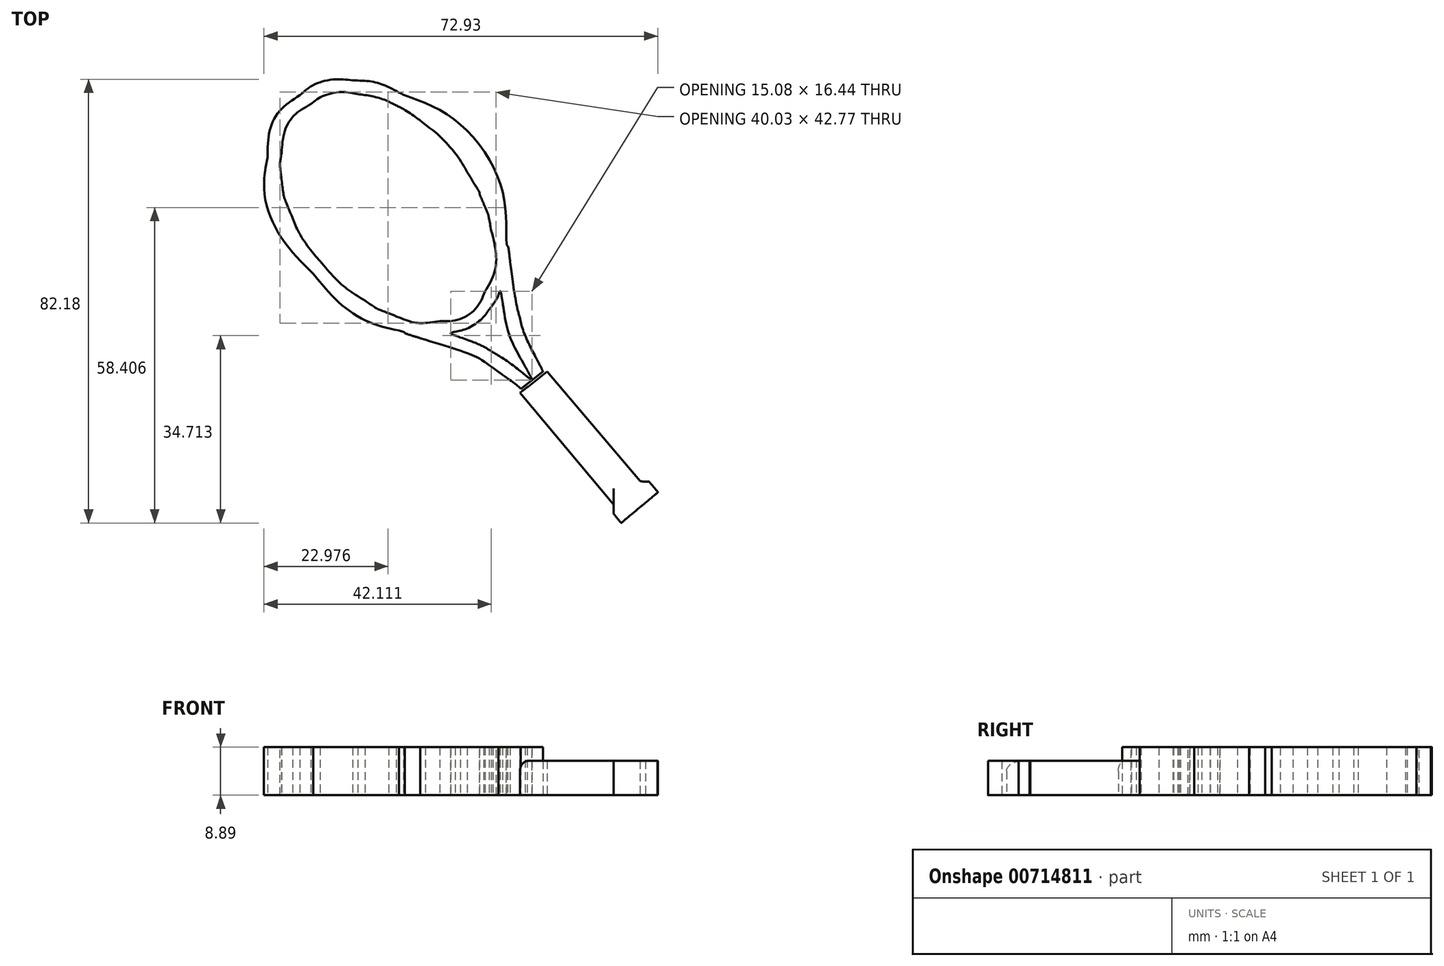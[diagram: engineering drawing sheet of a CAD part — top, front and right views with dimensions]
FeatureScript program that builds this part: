
annotation { "Feature Type Name" : "Feature", "Feature Type Description" : "" }
export const myFeature = defineFeature(function(context is Context, id is Id, definition is map)
    precondition{}
    {
        {
            var Q0;
            Q0=qCreatedBy(makeId("Top.planeOp"),FACE);
            var sketch = newSketch(context, id + "F0", { "sketchPlane" : qUnion([Q0])});
            skFitSpline(sketch, "E0", {"points": [v(14.84, -42.27) * mm, v(14.16, -41.44) * mm, v(14.13, -41.38) * mm, v(14.13, -40.56) * mm]});
            skFitSpline(sketch, "E1", {"points": [v(-3.07, -18.31) * mm, v(-3.2, -18.11) * mm, v(-5.86, -16.05) * mm, v(-7.2, -15.14) * mm]});
            skFitSpline(sketch, "E2", {"points": [v(-7.2, -15.14) * mm, v(-10.76, -12.67) * mm, v(-13.73, -11.39) * mm, v(-21.65, -8.9) * mm]});
            skFitSpline(sketch, "E3", {"points": [v(-21.65, -8.9) * mm, v(-23.19, -8.42) * mm, v(-24.48, -7.97) * mm, v(-24.53, -7.9) * mm]});
            skFitSpline(sketch, "E4", {"points": [v(-24.53, -7.9) * mm, v(-24.57, -7.83) * mm, v(-25.07, -7.64) * mm, v(-25.63, -7.48) * mm]});
            skFitSpline(sketch, "E5", {"points": [v(-25.63, -7.48) * mm, v(-31.35, -5.83) * mm, v(-36.86, -2.17) * mm, v(-41.46, 3.02) * mm]});
            skFitSpline(sketch, "E6", {"points": [v(-41.46, 3.02) * mm, v(-47.35, 9.65) * mm, v(-50.52, 17.71) * mm, v(-49.94, 24.59) * mm]});
            skFitSpline(sketch, "E7", {"points": [v(-49.94, 24.59) * mm, v(-49.52, 29.6) * mm, v(-47.6, 33.3) * mm, v(-43.94, 36.1) * mm]});
            skFitSpline(sketch, "E8", {"points": [v(-43.94, 36.1) * mm, v(-41.54, 37.93) * mm, v(-37.63, 39.02) * mm, v(-34.19, 38.83) * mm]});
            skFitSpline(sketch, "E9", {"points": [v(-34.19, 38.83) * mm, v(-30.86, 38.64) * mm, v(-28.26, 37.91) * mm, v(-24.79, 36.19) * mm]});
            skFitSpline(sketch, "E10", {"points": [v(-24.79, 36.19) * mm, v(-14.97, 31.3) * mm, v(-6.96, 20.04) * mm, v(-5.75, 9.4) * mm]});
            skFitSpline(sketch, "E11", {"points": [v(-5.75, 9.4) * mm, v(-5.68, 8.77) * mm, v(-5.56, 8.22) * mm, v(-5.5, 8.17) * mm]});
            skFitSpline(sketch, "E12", {"points": [v(-5.5, 8.17) * mm, v(-5.43, 8.13) * mm, v(-5.2, 6.8) * mm, v(-5, 5.21) * mm]});
            skFitSpline(sketch, "E13", {"points": [v(-5, 5.21) * mm, v(-4.54, 1.52) * mm, v(-3.77, -3) * mm, v(-3.29, -4.94) * mm]});
            skFitSpline(sketch, "E14", {"points": [v(-3.29, -4.94) * mm, v(-2.77, -6.97) * mm, v(-1.72, -9.61) * mm, v(-0.3, -12.38) * mm]});
            skFitSpline(sketch, "E15", {"points": [v(-0.3, -12.38) * mm, v(1.04, -15.03) * mm, v(1.07, -15.08) * mm, v(1.34, -14.85) * mm]});
            skFitSpline(sketch, "E16", {"points": [v(19.03, -35.32) * mm, v(19.21, -35.39) * mm, v(19.66, -35.44) * mm, v(20.03, -35.44) * mm]});
            skFitSpline(sketch, "E17", {"points": [v(20.03, -35.44) * mm, v(20.7, -35.44) * mm, v(20.71, -35.46) * mm, v(21.53, -36.43) * mm]});
            skFitSpline(sketch, "E18", {"points": [v(21.53, -36.43) * mm, v(21.99, -36.97) * mm, v(22.32, -37.46) * mm, v(22.26, -37.5) * mm]});
            skFitSpline(sketch, "E19", {"points": [v(22.26, -37.5) * mm, v(22.2, -37.56) * mm, v(20.8, -38.73) * mm, v(19.14, -40.1) * mm]});
            skFitSpline(sketch, "E20", {"points": [v(19.14, -40.1) * mm, v(17.48, -41.5) * mm, v(16, -42.74) * mm, v(15.83, -42.88) * mm]});
            skFitSpline(sketch, "E21", {"points": [v(15.83, -42.88) * mm, v(15.55, -43.13) * mm, v(15.54, -43.13) * mm, v(14.84, -42.27) * mm]});
            skLineSegment(sketch, "E22", {"start": v(14.13, -40.56) * mm, "end": v(14.13, -39.71) * mm});
            skFitSpline(sketch, "E23", {"points": [v(-1.88, -14.79) * mm, v(-4.5, -9.95) * mm, v(-5.63, -6.78) * mm, v(-6.46, -2.02) * mm]});
            skFitSpline(sketch, "E24", {"points": [v(-6.46, -2.02) * mm, v(-6.63, -1.02) * mm, v(-6.81, -0.2) * mm, v(-6.87, -0.2) * mm]});
            skFitSpline(sketch, "E25", {"points": [v(-6.87, -0.2) * mm, v(-6.92, -0.2) * mm, v(-7.03, -0.4) * mm, v(-7.11, -0.65) * mm]});
            skFitSpline(sketch, "E26", {"points": [v(-7.11, -0.65) * mm, v(-7.33, -1.27) * mm, v(-8.14, -2.58) * mm, v(-8.94, -3.6) * mm]});
            skFitSpline(sketch, "E27", {"points": [v(-8.94, -3.6) * mm, v(-10.3, -5.33) * mm, v(-12.99, -7.1) * mm, v(-15.18, -7.7) * mm]});
            skFitSpline(sketch, "E28", {"points": [v(-15.18, -7.7) * mm, v(-15.65, -7.82) * mm, v(-16.03, -7.97) * mm, v(-16.03, -8.01) * mm]});
            skFitSpline(sketch, "E29", {"points": [v(-16.03, -8.01) * mm, v(-16.03, -8.06) * mm, v(-15.22, -8.4) * mm, v(-14.22, -8.76) * mm]});
            skFitSpline(sketch, "E30", {"points": [v(-14.22, -8.76) * mm, v(-11.55, -9.74) * mm, v(-9.91, -10.49) * mm, v(-8.21, -11.5) * mm]});
            skFitSpline(sketch, "E31", {"points": [v(-8.21, -11.5) * mm, v(-6.48, -12.55) * mm, v(-4.04, -14.26) * mm, v(-2.27, -15.68) * mm]});
            skFitSpline(sketch, "E32", {"points": [v(-2.27, -15.68) * mm, v(-1.6, -16.22) * mm, v(-1.02, -16.64) * mm, v(-1, -16.6) * mm]});
            skFitSpline(sketch, "E33", {"points": [v(-1, -16.6) * mm, v(-0.96, -16.57) * mm, v(-1.36, -15.76) * mm, v(-1.88, -14.79) * mm]});
            skFitSpline(sketch, "E34", {"points": [v(-18.02, -5.76) * mm, v(-14.5, -5.4) * mm, v(-11.26, -3.26) * mm, v(-9.7, -0.23) * mm]});
            skFitSpline(sketch, "E35", {"points": [v(-9.7, -0.23) * mm, v(-8.02, 3) * mm, v(-7.63, 6.58) * mm, v(-8.5, 10.97) * mm]});
            skFitSpline(sketch, "E36", {"points": [v(-8.5, 10.97) * mm, v(-9.04, 13.74) * mm, v(-9.2, 14.3) * mm, v(-9.94, 16.01) * mm]});
            skFitSpline(sketch, "E37", {"points": [v(-9.94, 16.01) * mm, v(-10.35, 16.98) * mm, v(-10.69, 17.82) * mm, v(-10.69, 17.89) * mm]});
            skFitSpline(sketch, "E38", {"points": [v(-10.69, 17.89) * mm, v(-10.69, 18.02) * mm, v(-11.6, 19.6) * mm, v(-12.95, 21.8) * mm]});
            skFitSpline(sketch, "E39", {"points": [v(-12.95, 21.8) * mm, v(-14.73, 24.72) * mm, v(-18.08, 28.51) * mm, v(-20.73, 30.63) * mm]});
            skFitSpline(sketch, "E40", {"points": [v(-20.73, 30.63) * mm, v(-22.05, 31.68) * mm, v(-25.01, 33.64) * mm, v(-26.11, 34.18) * mm]});
            skFitSpline(sketch, "E41", {"points": [v(-26.11, 34.18) * mm, v(-28.1, 35.16) * mm, v(-30.67, 35.92) * mm, v(-33.24, 36.28) * mm]});
            skFitSpline(sketch, "E42", {"points": [v(-33.24, 36.28) * mm, v(-36.04, 36.68) * mm, v(-39.75, 35.9) * mm, v(-41.92, 34.45) * mm]});
            skFitSpline(sketch, "E43", {"points": [v(-41.92, 34.45) * mm, v(-44.96, 32.42) * mm, v(-46.77, 29.4) * mm, v(-47.36, 25.4) * mm]});
            skFitSpline(sketch, "E44", {"points": [v(-47.36, 25.4) * mm, v(-47.63, 23.56) * mm, v(-47.63, 22.79) * mm, v(-47.37, 20.67) * mm]});
            skFitSpline(sketch, "E45", {"points": [v(-47.37, 20.67) * mm, v(-47.03, 17.97) * mm, v(-46.62, 16.51) * mm, v(-45.27, 13.3) * mm]});
            skFitSpline(sketch, "E46", {"points": [v(-45.27, 13.3) * mm, v(-44.32, 11.03) * mm, v(-42.16, 7.65) * mm, v(-40.2, 5.38) * mm]});
            skFitSpline(sketch, "E47", {"points": [v(-40.2, 5.38) * mm, v(-37.55, 2.29) * mm, v(-35.22, 0.23) * mm, v(-31.93, -1.95) * mm]});
            skFitSpline(sketch, "E48", {"points": [v(-31.93, -1.95) * mm, v(-29.88, -3.3) * mm, v(-29.47, -3.52) * mm, v(-27.49, -4.29) * mm]});
            skFitSpline(sketch, "E49", {"points": [v(-27.49, -4.29) * mm, v(-23.61, -5.78) * mm, v(-21.51, -6.11) * mm, v(-18.02, -5.76) * mm]});
            skLineSegment(sketch, "E50", {"start": v(-18.02, -5.76) * mm, "end": v(-18.02, -5.76) * mm});
            skLineSegment(sketch, "E51", {"start": v(-3.07, -18.31) * mm, "end": v(1.34, -14.85) * mm});
            skLineSegment(sketch, "E52", {"start": v(-3.2, -19.01) * mm, "end": v(14.13, -39.71) * mm});
            skLineSegment(sketch, "E53", {"start": v(-3.07, -18.31) * mm, "end": v(-3.2, -19.01) * mm});
            skLineSegment(sketch, "E54", {"start": v(-3.2, -19.01) * mm, "end": v(1.84, -15.07) * mm});
            skLineSegment(sketch, "E55", {"start": v(1.84, -15.07) * mm, "end": v(19.03, -35.32) * mm});
            skLineSegment(sketch, "E56", {"start": v(-2.73, -18.65) * mm, "end": v(-3.07, -18.31) * mm});
            skSolve(sketch);
        }
        {
            var Q0;
            {var subQ4=sQuery(id+"F0.wireOp",EDGE,"E1");Q0=makeQuery(id+"F0.imprint","IMPRINT",FACE,{"disambiguationData":[TD([[makeQuery(id+"F0.imprint","IMPRINT",EDGE,{"derivedFrom":subQ4}),-1.0]])]});}
            extrude(context, id + "F1", {"entities" : qUnion([Q0]), "depth" : 8.9 * mm, "offsetDistance" : 25.4 * mm});
        }
        {
            var Q0;
            Q0=makeQuery(id+"F0.imprint","IMPRINT",FACE,{"disambiguationData":[TD([[makeQuery(id+"F0.imprint","IMPRINT",EDGE,{"derivedFrom":sQuery(id+"F0.wireOp",EDGE,"E0")}),-1.0]])]});
            extrude(context, id + "F2", {"entities" : qUnion([Q0]), "operationType" : NewBodyOperationType.ADD, "depth" : 6.35 * mm, "offsetDistance" : 25.4 * mm});
        }
        {
            var Q0;
            Q0=makeQuery(id+"F2.opExtrude","CAP_EDGE",EDGE,{"disambiguationData":[OSD([sQuery(id+"F0.wireOp",EDGE,"E52")])],"isStart":false});
            fillet(context, id + "F3", {"entities" : qUnion([Q0]), "radius" : 1.9 * mm, "tangentPropagation" : true, "allowEdgeOverflow" : false});
        }
    });
